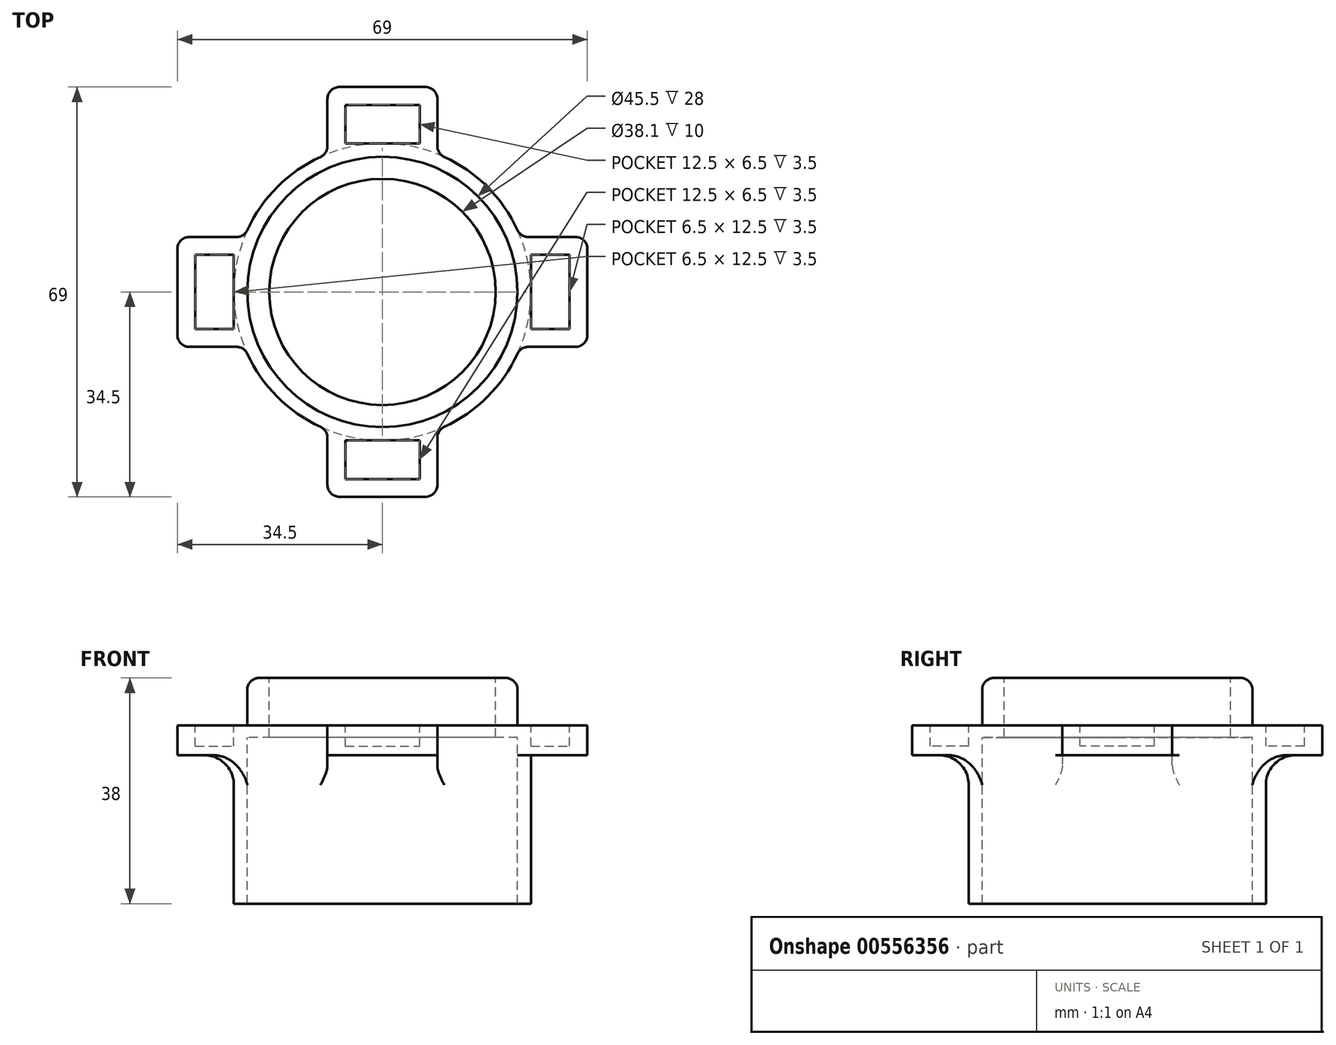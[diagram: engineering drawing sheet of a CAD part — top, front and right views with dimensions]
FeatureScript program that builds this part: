
annotation { "Feature Type Name" : "Feature", "Feature Type Description" : "" }
export const myFeature = defineFeature(function(context is Context, id is Id, definition is map)
    precondition{}
    {
        {
            var Q0;
            Q0=qCreatedBy(makeId("Top.planeOp"),FACE);
            var sketch = newSketch(context, id + "F0", { "sketchPlane" : qUnion([Q0])});
            skCircle(sketch, "E0", {"center": v(0, 0) * mm, "radius": 31.75 * mm, "construction": true});
            skCircle(sketch, "E1", {"center": v(0, 0) * mm, "radius": 22.75 * mm});
            skLineSegment(sketch, "E2.bottom", {"start": v(25, 6.25) * mm, "end": v(31.5, 6.25) * mm});
            skLineSegment(sketch, "E2.top", {"start": v(25, -6.25) * mm, "end": v(31.5, -6.25) * mm});
            skLineSegment(sketch, "E2.left", {"start": v(25, 6.25) * mm, "end": v(25, -6.25) * mm});
            skLineSegment(sketch, "E2.right", {"start": v(31.5, 6.25) * mm, "end": v(31.5, -6.25) * mm});
            skPoint(sketch, "E3", {"position": v(25, 0) * mm});
            skCircle(sketch, "E4", {"center": v(0, 0) * mm, "radius": 25 * mm});
            skLineSegment(sketch, "E5.bottom", {"start": v(-31.5, 6.25) * mm, "end": v(-25, 6.25) * mm});
            skLineSegment(sketch, "E5.top", {"start": v(-31.5, -6.25) * mm, "end": v(-25, -6.25) * mm});
            skLineSegment(sketch, "E5.left", {"start": v(-31.5, 6.25) * mm, "end": v(-31.5, -6.25) * mm});
            skLineSegment(sketch, "E5.right", {"start": v(-25, 6.25) * mm, "end": v(-25, -6.25) * mm});
            skPoint(sketch, "E6", {"position": v(-25, 0) * mm});
            skLineSegment(sketch, "E7.bottom", {"start": v(-34.5, 9.25) * mm, "end": v(34.5, 9.25) * mm});
            skLineSegment(sketch, "E7.top", {"start": v(-34.5, -9.25) * mm, "end": v(34.5, -9.25) * mm});
            skLineSegment(sketch, "E7.left", {"start": v(-34.5, 9.25) * mm, "end": v(-34.5, -9.25) * mm});
            skLineSegment(sketch, "E7.right", {"start": v(34.5, 9.25) * mm, "end": v(34.5, -9.25) * mm});
            skCircle(sketch, "E8", {"center": v(0, 0) * mm, "radius": 19.05 * mm});
            skLineSegment(sketch, "E9.bottom", {"start": v(-9.25, -34.5) * mm, "end": v(9.25, -34.5) * mm});
            skLineSegment(sketch, "E9.top", {"start": v(-9.25, 34.5) * mm, "end": v(9.25, 34.5) * mm});
            skLineSegment(sketch, "E9.left", {"start": v(-9.25, -34.5) * mm, "end": v(-9.25, 34.5) * mm});
            skLineSegment(sketch, "E9.right", {"start": v(9.25, -34.5) * mm, "end": v(9.25, 34.5) * mm});
            skLineSegment(sketch, "E10.bottom", {"start": v(-6.25, 31.5) * mm, "end": v(6.25, 31.5) * mm});
            skLineSegment(sketch, "E10.top", {"start": v(-6.25, 25) * mm, "end": v(6.25, 25) * mm});
            skLineSegment(sketch, "E10.left", {"start": v(-6.25, 31.5) * mm, "end": v(-6.25, 25) * mm});
            skLineSegment(sketch, "E10.right", {"start": v(6.25, 31.5) * mm, "end": v(6.25, 25) * mm});
            skLineSegment(sketch, "E11.bottom", {"start": v(-6.25, -25) * mm, "end": v(6.25, -25) * mm});
            skLineSegment(sketch, "E11.top", {"start": v(-6.25, -31.5) * mm, "end": v(6.25, -31.5) * mm});
            skLineSegment(sketch, "E11.left", {"start": v(-6.25, -25) * mm, "end": v(-6.25, -31.5) * mm});
            skLineSegment(sketch, "E11.right", {"start": v(6.25, -25) * mm, "end": v(6.25, -31.5) * mm});
            skPoint(sketch, "E12", {"position": v(0, 25) * mm});
            skSolve(sketch);
        }
        {
            var Q0;
            {var subQ0=sQuery(id+"F0.wireOp",EDGE,"E5.bottom");Q0=makeQuery(id+"F0.imprint","IMPRINT",FACE,{"disambiguationData":[TD([[makeQuery(id+"F0.imprint","IMPRINT",EDGE,{"derivedFrom":subQ0}),1.0]])]});}
            var Q1;
            {var subQ4=sQuery(id+"F0.wireOp",EDGE,"E2.bottom");Q1=makeQuery(id+"F0.imprint","IMPRINT",FACE,{"disambiguationData":[TD([[makeQuery(id+"F0.imprint","IMPRINT",EDGE,{"derivedFrom":subQ4}),1.0]])]});}
            var Q2;
            {var subQ0=sQuery(id+"F0.wireOp",EDGE,"E7.top");var subQ1=sQuery(id+"F0.wireOp",EDGE,"9AU1a6xc-WkkM-5iDV-fBZs-smRrCXbzpLaA");var subQ2=makeQuery(id+"F0.imprint","INTERSECT",VERTEX,{"disambiguationData":[OD(0.0)],"derivedFrom":[subQ1,subQ0]});Q2=makeQuery(id+"F0.imprint","IMPRINT",FACE,{"disambiguationData":[TD([[makeQuery(id+"F0.imprint","IMPRINT",EDGE,{"disambiguationData":[TD([[subQ2,-1.0]])],"derivedFrom":subQ1}),-1.0]])]});}
            var Q3;
            {var subQ0=sQuery(id+"F0.wireOp",EDGE,"E7.bottom");var subQ3=sQuery(id+"F0.wireOp",EDGE,"9AU1a6xc-WkkM-5iDV-fBZs-smRrCXbzpLaA");var subQ4=makeQuery(id+"F0.imprint","INTERSECT",VERTEX,{"disambiguationData":[OD(1.0)],"derivedFrom":[subQ3,subQ0]});Q3=makeQuery(id+"F0.imprint","IMPRINT",FACE,{"disambiguationData":[TD([[makeQuery(id+"F0.imprint","IMPRINT",EDGE,{"disambiguationData":[TD([[subQ4,1.0]])],"derivedFrom":subQ3}),-1.0]])]});}
            var Q4;
            {var subQ0=sQuery(id+"F0.wireOp",EDGE,"E7.bottom");var subQ1=sQuery(id+"F0.wireOp",EDGE,"9AU1a6xc-WkkM-5iDV-fBZs-smRrCXbzpLaA");var subQ2=makeQuery(id+"F0.imprint","INTERSECT",VERTEX,{"disambiguationData":[OD(0.0)],"derivedFrom":[subQ1,subQ0]});Q4=makeQuery(id+"F0.imprint","IMPRINT",FACE,{"disambiguationData":[TD([[makeQuery(id+"F0.imprint","IMPRINT",EDGE,{"disambiguationData":[TD([[subQ2,1.0]])],"derivedFrom":subQ1}),-1.0]])]});}
            var Q5;
            {var subQ0=sQuery(id+"F0.wireOp",EDGE,"E7.bottom");var subQ3=sQuery(id+"F0.wireOp",EDGE,"9AU1a6xc-WkkM-5iDV-fBZs-smRrCXbzpLaA");var subQ4=makeQuery(id+"F0.imprint","INTERSECT",VERTEX,{"disambiguationData":[OD(0.0)],"derivedFrom":[subQ3,subQ0]});Q5=makeQuery(id+"F0.imprint","IMPRINT",FACE,{"disambiguationData":[TD([[makeQuery(id+"F0.imprint","IMPRINT",EDGE,{"disambiguationData":[TD([[subQ4,-1.0]])],"derivedFrom":subQ3}),-1.0]])]});}
            var Q6;
            {var subQ0=sQuery(id+"F0.wireOp",EDGE,"E7.bottom");var subQ1=sQuery(id+"F0.wireOp",EDGE,"9AU1a6xc-WkkM-5iDV-fBZs-smRrCXbzpLaA");var subQ2=makeQuery(id+"F0.imprint","INTERSECT",VERTEX,{"disambiguationData":[OD(0.0)],"derivedFrom":[subQ1,subQ0]});Q6=makeQuery(id+"F0.imprint","IMPRINT",FACE,{"disambiguationData":[TD([[makeQuery(id+"F0.imprint","IMPRINT",EDGE,{"disambiguationData":[TD([[subQ2,-1.0]])],"derivedFrom":subQ1}),1.0]])]});}
            var Q7;
            {var subQ0=sQuery(id+"F0.wireOp",EDGE,"E7.bottom");var subQ1=sQuery(id+"F0.wireOp",EDGE,"9AU1a6xc-WkkM-5iDV-fBZs-smRrCXbzpLaA");var subQ2=makeQuery(id+"F0.imprint","INTERSECT",VERTEX,{"disambiguationData":[OD(1.0)],"derivedFrom":[subQ1,subQ0]});Q7=makeQuery(id+"F0.imprint","IMPRINT",FACE,{"disambiguationData":[TD([[makeQuery(id+"F0.imprint","IMPRINT",EDGE,{"disambiguationData":[TD([[subQ2,1.0]])],"derivedFrom":subQ1}),1.0]])]});}
            var Q8;
            {var subQ0=sQuery(id+"F0.wireOp",EDGE,"E7.bottom");var subQ1=sQuery(id+"F0.wireOp",EDGE,"9AU1a6xc-WkkM-5iDV-fBZs-smRrCXbzpLaA");var subQ2=makeQuery(id+"F0.imprint","INTERSECT",VERTEX,{"disambiguationData":[OD(0.0)],"derivedFrom":[subQ1,subQ0]});Q8=makeQuery(id+"F0.imprint","IMPRINT",FACE,{"disambiguationData":[TD([[makeQuery(id+"F0.imprint","IMPRINT",EDGE,{"disambiguationData":[TD([[subQ2,1.0]])],"derivedFrom":subQ1}),1.0]])]});}
            var Q9;
            {var subQ0=sQuery(id+"F0.wireOp",EDGE,"E7.top");var subQ1=sQuery(id+"F0.wireOp",EDGE,"9AU1a6xc-WkkM-5iDV-fBZs-smRrCXbzpLaA");var subQ2=makeQuery(id+"F0.imprint","INTERSECT",VERTEX,{"disambiguationData":[OD(0.0)],"derivedFrom":[subQ1,subQ0]});Q9=makeQuery(id+"F0.imprint","IMPRINT",FACE,{"disambiguationData":[TD([[makeQuery(id+"F0.imprint","IMPRINT",EDGE,{"disambiguationData":[TD([[subQ2,-1.0]])],"derivedFrom":subQ1}),1.0]])]});}
            var Q10;
            {var subQ1=sQuery(id+"F0.wireOp",EDGE,"E5.bottom");Q10=makeQuery(id+"F0.imprint","IMPRINT",FACE,{"disambiguationData":[TD([[makeQuery(id+"F0.imprint","IMPRINT",EDGE,{"derivedFrom":subQ1}),-1.0]])]});}
            var Q11;
            {var subQ3=sQuery(id+"F0.wireOp",EDGE,"E2.bottom");Q11=makeQuery(id+"F0.imprint","IMPRINT",FACE,{"disambiguationData":[TD([[makeQuery(id+"F0.imprint","IMPRINT",EDGE,{"derivedFrom":subQ3}),-1.0]])]});}
            var Q12;
            {var subQ0=sQuery(id+"F0.wireOp",EDGE,"E7.bottom");var subQ1=sQuery(id+"F0.wireOp",EDGE,"E1");var subQ2=makeQuery(id+"F0.imprint","INTERSECT",VERTEX,{"disambiguationData":[OD(0.0)],"derivedFrom":[subQ1,subQ0]});Q12=makeQuery(id+"F0.imprint","IMPRINT",FACE,{"disambiguationData":[TD([[makeQuery(id+"F0.imprint","IMPRINT",EDGE,{"disambiguationData":[TD([[subQ2,1.0]])],"derivedFrom":subQ1}),-1.0]])]});}
            var Q13;
            {var subQ4=sQuery(id+"F0.wireOp",EDGE,"E7.bottom");var subQ5=sQuery(id+"F0.wireOp",EDGE,"E1");var subQ6=makeQuery(id+"F0.imprint","INTERSECT",VERTEX,{"disambiguationData":[OD(0.0)],"derivedFrom":[subQ5,subQ4]});Q13=makeQuery(id+"F0.imprint","IMPRINT",FACE,{"disambiguationData":[TD([[makeQuery(id+"F0.imprint","IMPRINT",EDGE,{"disambiguationData":[TD([[subQ6,-1.0]])],"derivedFrom":subQ5}),-1.0]])]});}
            var Q14;
            {var subQ4=sQuery(id+"F0.wireOp",EDGE,"E7.bottom");var subQ5=sQuery(id+"F0.wireOp",EDGE,"E1");var subQ6=makeQuery(id+"F0.imprint","INTERSECT",VERTEX,{"disambiguationData":[OD(1.0)],"derivedFrom":[subQ5,subQ4]});Q14=makeQuery(id+"F0.imprint","IMPRINT",FACE,{"disambiguationData":[TD([[makeQuery(id+"F0.imprint","IMPRINT",EDGE,{"disambiguationData":[TD([[subQ6,1.0]])],"derivedFrom":subQ5}),-1.0]])]});}
            var Q15;
            {var subQ0=sQuery(id+"F0.wireOp",EDGE,"E7.top");var subQ1=sQuery(id+"F0.wireOp",EDGE,"E1");var subQ2=makeQuery(id+"F0.imprint","INTERSECT",VERTEX,{"disambiguationData":[OD(0.0)],"derivedFrom":[subQ1,subQ0]});Q15=makeQuery(id+"F0.imprint","IMPRINT",FACE,{"disambiguationData":[TD([[makeQuery(id+"F0.imprint","IMPRINT",EDGE,{"disambiguationData":[TD([[subQ2,-1.0]])],"derivedFrom":subQ1}),-1.0]])]});}
            var Q16;
            {var subQ0=sQuery(id+"F0.wireOp",EDGE,"E7.bottom");var subQ3=sQuery(id+"F0.wireOp",EDGE,"E1");var subQ4=makeQuery(id+"F0.imprint","INTERSECT",VERTEX,{"disambiguationData":[OD(1.0)],"derivedFrom":[subQ3,subQ0]});Q16=makeQuery(id+"F0.imprint","IMPRINT",FACE,{"disambiguationData":[TD([[makeQuery(id+"F0.imprint","IMPRINT",EDGE,{"disambiguationData":[TD([[subQ4,-1.0]])],"derivedFrom":subQ3}),-1.0]])]});}
            var Q17;
            {var subQ1=sQuery(id+"F0.wireOp",EDGE,"E9.top");Q17=makeQuery(id+"F0.imprint","IMPRINT",FACE,{"disambiguationData":[TD([[makeQuery(id+"F0.imprint","IMPRINT",EDGE,{"derivedFrom":subQ1}),-1.0]])]});}
            var Q18;
            Q18=makeQuery(id+"F0.imprint","IMPRINT",FACE,{"disambiguationData":[TD([[makeQuery(id+"F0.imprint","IMPRINT",EDGE,{"derivedFrom":sQuery(id+"F0.wireOp",EDGE,"E10.bottom")}),-1.0]])]});
            var Q19;
            {var subQ3=sQuery(id+"F0.wireOp",EDGE,"E1");var subQ5=sQuery(id+"F0.wireOp",EDGE,"E9.right");var subQ6=makeQuery(id+"F0.imprint","INTERSECT",VERTEX,{"disambiguationData":[OD(0.0)],"derivedFrom":[subQ3,subQ5]});Q19=makeQuery(id+"F0.imprint","IMPRINT",FACE,{"disambiguationData":[TD([[makeQuery(id+"F0.imprint","IMPRINT",EDGE,{"disambiguationData":[TD([[subQ6,-1.0]])],"derivedFrom":subQ3}),-1.0]])]});}
            var Q20;
            {var subQ0=sQuery(id+"F0.wireOp",EDGE,"E9.right");var subQ1=sQuery(id+"F0.wireOp",EDGE,"E1");var subQ2=makeQuery(id+"F0.imprint","INTERSECT",VERTEX,{"disambiguationData":[OD(1.0)],"derivedFrom":[subQ1,subQ0]});Q20=makeQuery(id+"F0.imprint","IMPRINT",FACE,{"disambiguationData":[TD([[makeQuery(id+"F0.imprint","IMPRINT",EDGE,{"disambiguationData":[TD([[subQ2,-1.0]])],"derivedFrom":subQ1}),-1.0]])]});}
            var Q21;
            {var subQ4=sQuery(id+"F0.wireOp",EDGE,"E9.left");var subQ6=sQuery(id+"F0.wireOp",EDGE,"E1");var subQ7=makeQuery(id+"F0.imprint","INTERSECT",VERTEX,{"disambiguationData":[OD(1.0)],"derivedFrom":[subQ6,subQ4]});Q21=makeQuery(id+"F0.imprint","IMPRINT",FACE,{"disambiguationData":[TD([[makeQuery(id+"F0.imprint","IMPRINT",EDGE,{"disambiguationData":[TD([[subQ7,-1.0]])],"derivedFrom":subQ6}),-1.0]])]});}
            var Q22;
            {var subQ1=sQuery(id+"F0.wireOp",EDGE,"E9.bottom");Q22=makeQuery(id+"F0.imprint","IMPRINT",FACE,{"disambiguationData":[TD([[makeQuery(id+"F0.imprint","IMPRINT",EDGE,{"derivedFrom":subQ1}),1.0]])]});}
            var Q23;
            Q23=makeQuery(id+"F0.imprint","IMPRINT",FACE,{"disambiguationData":[TD([[makeQuery(id+"F0.imprint","IMPRINT",EDGE,{"derivedFrom":sQuery(id+"F0.wireOp",EDGE,"E11.top")}),1.0]])]});
            extrude(context, id + "F1", {"entities" : qUnion([Q0, Q1, Q2, Q3, Q4, Q5, Q6, Q7, Q8, Q9, Q10, Q11, Q12, Q13, Q14, Q15, Q16, Q17, Q18, Q19, Q20, Q21, Q22, Q23]), "oppositeDirection" : true, "depth" : 5 * mm, "offsetDistance" : 25 * mm});
        }
        {
            var Q0;
            {var subQ0=sQuery(id+"F0.wireOp",EDGE,"E7.bottom");var subQ1=sQuery(id+"F0.wireOp",EDGE,"E1");var subQ2=makeQuery(id+"F0.imprint","INTERSECT",VERTEX,{"disambiguationData":[OD(0.0)],"derivedFrom":[subQ1,subQ0]});Q0=makeQuery(id+"F0.imprint","IMPRINT",FACE,{"disambiguationData":[TD([[makeQuery(id+"F0.imprint","IMPRINT",EDGE,{"disambiguationData":[TD([[subQ2,1.0]])],"derivedFrom":subQ1}),1.0]])]});}
            var Q1;
            {var subQ0=sQuery(id+"F0.wireOp",EDGE,"E7.bottom");var subQ1=sQuery(id+"F0.wireOp",EDGE,"E1");var subQ2=makeQuery(id+"F0.imprint","INTERSECT",VERTEX,{"disambiguationData":[OD(0.0)],"derivedFrom":[subQ1,subQ0]});Q1=makeQuery(id+"F0.imprint","IMPRINT",FACE,{"disambiguationData":[TD([[makeQuery(id+"F0.imprint","IMPRINT",EDGE,{"disambiguationData":[TD([[subQ2,-1.0]])],"derivedFrom":subQ1}),1.0]])]});}
            var Q2;
            {var subQ0=sQuery(id+"F0.wireOp",EDGE,"E7.top");var subQ1=sQuery(id+"F0.wireOp",EDGE,"E1");var subQ2=makeQuery(id+"F0.imprint","INTERSECT",VERTEX,{"disambiguationData":[OD(0.0)],"derivedFrom":[subQ1,subQ0]});Q2=makeQuery(id+"F0.imprint","IMPRINT",FACE,{"disambiguationData":[TD([[makeQuery(id+"F0.imprint","IMPRINT",EDGE,{"disambiguationData":[TD([[subQ2,-1.0]])],"derivedFrom":subQ1}),1.0]])]});}
            var Q3;
            {var subQ0=sQuery(id+"F0.wireOp",EDGE,"E7.bottom");var subQ1=sQuery(id+"F0.wireOp",EDGE,"E1");var subQ2=makeQuery(id+"F0.imprint","INTERSECT",VERTEX,{"disambiguationData":[OD(1.0)],"derivedFrom":[subQ1,subQ0]});Q3=makeQuery(id+"F0.imprint","IMPRINT",FACE,{"disambiguationData":[TD([[makeQuery(id+"F0.imprint","IMPRINT",EDGE,{"disambiguationData":[TD([[subQ2,1.0]])],"derivedFrom":subQ1}),1.0]])]});}
            var Q4;
            {var subQ0=sQuery(id+"F0.wireOp",EDGE,"E9.right");var subQ1=sQuery(id+"F0.wireOp",EDGE,"E1");var subQ2=makeQuery(id+"F0.imprint","INTERSECT",VERTEX,{"disambiguationData":[OD(1.0)],"derivedFrom":[subQ1,subQ0]});Q4=makeQuery(id+"F0.imprint","IMPRINT",FACE,{"disambiguationData":[TD([[makeQuery(id+"F0.imprint","IMPRINT",EDGE,{"disambiguationData":[TD([[subQ2,-1.0]])],"derivedFrom":subQ1}),1.0]])]});}
            var Q5;
            {var subQ0=sQuery(id+"F0.wireOp",EDGE,"E9.left");var subQ1=sQuery(id+"F0.wireOp",EDGE,"E1");var subQ2=makeQuery(id+"F0.imprint","INTERSECT",VERTEX,{"disambiguationData":[OD(1.0)],"derivedFrom":[subQ1,subQ0]});Q5=makeQuery(id+"F0.imprint","IMPRINT",FACE,{"disambiguationData":[TD([[makeQuery(id+"F0.imprint","IMPRINT",EDGE,{"disambiguationData":[TD([[subQ2,-1.0]])],"derivedFrom":subQ1}),1.0]])]});}
            var Q6;
            {var subQ0=sQuery(id+"F0.wireOp",EDGE,"E9.right");var subQ1=sQuery(id+"F0.wireOp",EDGE,"E1");var subQ2=makeQuery(id+"F0.imprint","INTERSECT",VERTEX,{"disambiguationData":[OD(0.0)],"derivedFrom":[subQ1,subQ0]});Q6=makeQuery(id+"F0.imprint","IMPRINT",FACE,{"disambiguationData":[TD([[makeQuery(id+"F0.imprint","IMPRINT",EDGE,{"disambiguationData":[TD([[subQ2,-1.0]])],"derivedFrom":subQ1}),1.0]])]});}
            var Q7;
            {var subQ0=sQuery(id+"F0.wireOp",EDGE,"E7.bottom");var subQ1=sQuery(id+"F0.wireOp",EDGE,"E1");var subQ2=makeQuery(id+"F0.imprint","INTERSECT",VERTEX,{"disambiguationData":[OD(1.0)],"derivedFrom":[subQ1,subQ0]});Q7=makeQuery(id+"F0.imprint","IMPRINT",FACE,{"disambiguationData":[TD([[makeQuery(id+"F0.imprint","IMPRINT",EDGE,{"disambiguationData":[TD([[subQ2,-1.0]])],"derivedFrom":subQ1}),1.0]])]});}
            extrude(context, id + "F2", {"entities" : qUnion([Q0, Q1, Q2, Q3, Q4, Q5, Q6, Q7]), "operationType" : NewBodyOperationType.ADD, "oppositeDirection" : true, "depth" : 2 * mm, "offsetDistance" : 25 * mm});
        }
        {
            var Q0;
            {var subQ1=sQuery(id+"F0.wireOp",EDGE,"E5.bottom");Q0=makeQuery(id+"F0.imprint","IMPRINT",FACE,{"disambiguationData":[TD([[makeQuery(id+"F0.imprint","IMPRINT",EDGE,{"derivedFrom":subQ1}),-1.0]])]});}
            var Q1;
            {var subQ3=sQuery(id+"F0.wireOp",EDGE,"E2.bottom");Q1=makeQuery(id+"F0.imprint","IMPRINT",FACE,{"disambiguationData":[TD([[makeQuery(id+"F0.imprint","IMPRINT",EDGE,{"derivedFrom":subQ3}),-1.0]])]});}
            var Q2;
            Q2=makeQuery(id+"F0.imprint","IMPRINT",FACE,{"disambiguationData":[TD([[makeQuery(id+"F0.imprint","IMPRINT",EDGE,{"derivedFrom":sQuery(id+"F0.wireOp",EDGE,"E11.top")}),1.0]])]});
            var Q3;
            Q3=makeQuery(id+"F0.imprint","IMPRINT",FACE,{"disambiguationData":[TD([[makeQuery(id+"F0.imprint","IMPRINT",EDGE,{"derivedFrom":sQuery(id+"F0.wireOp",EDGE,"E10.bottom")}),-1.0]])]});
            extrude(context, id + "F3", {"entities" : qUnion([Q0, Q1, Q2, Q3]), "operationType" : NewBodyOperationType.REMOVE, "oppositeDirection" : true, "depth" : 3.5 * mm, "offsetDistance" : 25 * mm});
        }
        {
            var Q0;
            {var subQ0=sQuery(id+"F0.wireOp",EDGE,"E7.bottom");var subQ1=sQuery(id+"F0.wireOp",EDGE,"E1");var subQ2=makeQuery(id+"F0.imprint","INTERSECT",VERTEX,{"disambiguationData":[OD(0.0)],"derivedFrom":[subQ1,subQ0]});Q0=makeQuery(id+"F0.imprint","IMPRINT",FACE,{"disambiguationData":[TD([[makeQuery(id+"F0.imprint","IMPRINT",EDGE,{"disambiguationData":[TD([[subQ2,1.0]])],"derivedFrom":subQ1}),1.0]])]});}
            var Q1;
            {var subQ0=sQuery(id+"F0.wireOp",EDGE,"E7.bottom");var subQ1=sQuery(id+"F0.wireOp",EDGE,"E1");var subQ2=makeQuery(id+"F0.imprint","INTERSECT",VERTEX,{"disambiguationData":[OD(0.0)],"derivedFrom":[subQ1,subQ0]});Q1=makeQuery(id+"F0.imprint","IMPRINT",FACE,{"disambiguationData":[TD([[makeQuery(id+"F0.imprint","IMPRINT",EDGE,{"disambiguationData":[TD([[subQ2,-1.0]])],"derivedFrom":subQ1}),1.0]])]});}
            var Q2;
            {var subQ0=sQuery(id+"F0.wireOp",EDGE,"E7.bottom");var subQ1=sQuery(id+"F0.wireOp",EDGE,"E1");var subQ2=makeQuery(id+"F0.imprint","INTERSECT",VERTEX,{"disambiguationData":[OD(1.0)],"derivedFrom":[subQ1,subQ0]});Q2=makeQuery(id+"F0.imprint","IMPRINT",FACE,{"disambiguationData":[TD([[makeQuery(id+"F0.imprint","IMPRINT",EDGE,{"disambiguationData":[TD([[subQ2,1.0]])],"derivedFrom":subQ1}),1.0]])]});}
            var Q3;
            {var subQ0=sQuery(id+"F0.wireOp",EDGE,"E7.top");var subQ1=sQuery(id+"F0.wireOp",EDGE,"E1");var subQ2=makeQuery(id+"F0.imprint","INTERSECT",VERTEX,{"disambiguationData":[OD(0.0)],"derivedFrom":[subQ1,subQ0]});Q3=makeQuery(id+"F0.imprint","IMPRINT",FACE,{"disambiguationData":[TD([[makeQuery(id+"F0.imprint","IMPRINT",EDGE,{"disambiguationData":[TD([[subQ2,-1.0]])],"derivedFrom":subQ1}),1.0]])]});}
            var Q4;
            {var subQ0=sQuery(id+"F0.wireOp",EDGE,"E7.bottom");var subQ1=sQuery(id+"F0.wireOp",EDGE,"E1");var subQ2=makeQuery(id+"F0.imprint","INTERSECT",VERTEX,{"disambiguationData":[OD(1.0)],"derivedFrom":[subQ1,subQ0]});Q4=makeQuery(id+"F0.imprint","IMPRINT",FACE,{"disambiguationData":[TD([[makeQuery(id+"F0.imprint","IMPRINT",EDGE,{"disambiguationData":[TD([[subQ2,-1.0]])],"derivedFrom":subQ1}),1.0]])]});}
            var Q5;
            {var subQ0=sQuery(id+"F0.wireOp",EDGE,"E9.left");var subQ1=sQuery(id+"F0.wireOp",EDGE,"E1");var subQ2=makeQuery(id+"F0.imprint","INTERSECT",VERTEX,{"disambiguationData":[OD(1.0)],"derivedFrom":[subQ1,subQ0]});Q5=makeQuery(id+"F0.imprint","IMPRINT",FACE,{"disambiguationData":[TD([[makeQuery(id+"F0.imprint","IMPRINT",EDGE,{"disambiguationData":[TD([[subQ2,-1.0]])],"derivedFrom":subQ1}),1.0]])]});}
            var Q6;
            {var subQ0=sQuery(id+"F0.wireOp",EDGE,"E9.right");var subQ1=sQuery(id+"F0.wireOp",EDGE,"E1");var subQ2=makeQuery(id+"F0.imprint","INTERSECT",VERTEX,{"disambiguationData":[OD(1.0)],"derivedFrom":[subQ1,subQ0]});Q6=makeQuery(id+"F0.imprint","IMPRINT",FACE,{"disambiguationData":[TD([[makeQuery(id+"F0.imprint","IMPRINT",EDGE,{"disambiguationData":[TD([[subQ2,-1.0]])],"derivedFrom":subQ1}),1.0]])]});}
            var Q7;
            {var subQ0=sQuery(id+"F0.wireOp",EDGE,"E9.right");var subQ1=sQuery(id+"F0.wireOp",EDGE,"E1");var subQ2=makeQuery(id+"F0.imprint","INTERSECT",VERTEX,{"disambiguationData":[OD(0.0)],"derivedFrom":[subQ1,subQ0]});Q7=makeQuery(id+"F0.imprint","IMPRINT",FACE,{"disambiguationData":[TD([[makeQuery(id+"F0.imprint","IMPRINT",EDGE,{"disambiguationData":[TD([[subQ2,-1.0]])],"derivedFrom":subQ1}),1.0]])]});}
            extrude(context, id + "F4", {"entities" : qUnion([Q0, Q1, Q2, Q3, Q4, Q5, Q6, Q7]), "operationType" : NewBodyOperationType.ADD, "depth" : 8 * mm, "offsetDistance" : 25 * mm});
        }
        {
            var Q0;
            Q0=makeQuery(id+"F1.opExtrude","SWEPT_EDGE",EDGE,{"disambiguationData":[OSD([sQuery(id+"F0.wireOp",EDGE,"E7.bottom"),sQuery(id+"F0.wireOp",EDGE,"E7.left")])]});
            var Q1;
            {var subQ0=sQuery(id+"F0.wireOp",EDGE,"E7.bottom");var subQ1=sQuery(id+"F0.wireOp",EDGE,"E4");Q1=makeQuery(id+"F1.opExtrude","SWEPT_EDGE",EDGE,{"disambiguationData":[OSD([subQ1,subQ0]),TDD([makeQuery(id+"F0.imprint","INTERSECT",VERTEX,{"disambiguationData":[OD(1.0)],"derivedFrom":[subQ1,subQ0]})])]});}
            var Q2;
            Q2=makeQuery(id+"F1.opExtrude","SWEPT_EDGE",EDGE,{"disambiguationData":[OSD([sQuery(id+"F0.wireOp",EDGE,"E7.top"),sQuery(id+"F0.wireOp",EDGE,"E7.left")])]});
            var Q3;
            Q3=makeQuery(id+"F1.opExtrude","SWEPT_EDGE",EDGE,{"disambiguationData":[OSD([sQuery(id+"F0.wireOp",EDGE,"E7.bottom"),sQuery(id+"F0.wireOp",EDGE,"E7.right")])]});
            var Q4;
            {var subQ0=sQuery(id+"F0.wireOp",EDGE,"E7.top");var subQ1=sQuery(id+"F0.wireOp",EDGE,"E4");Q4=makeQuery(id+"F1.opExtrude","SWEPT_EDGE",EDGE,{"disambiguationData":[OSD([subQ1,subQ0]),TDD([makeQuery(id+"F0.imprint","INTERSECT",VERTEX,{"disambiguationData":[OD(1.0)],"derivedFrom":[subQ1,subQ0]})])]});}
            var Q5;
            Q5=makeQuery(id+"F1.opExtrude","SWEPT_EDGE",EDGE,{"disambiguationData":[OSD([sQuery(id+"F0.wireOp",EDGE,"E7.top"),sQuery(id+"F0.wireOp",EDGE,"E7.right")])]});
            var Q6;
            {var subQ0=sQuery(id+"F0.wireOp",EDGE,"E7.top");var subQ1=sQuery(id+"F0.wireOp",EDGE,"E4");Q6=makeQuery(id+"F1.opExtrude","SWEPT_EDGE",EDGE,{"disambiguationData":[OSD([subQ1,subQ0]),TDD([makeQuery(id+"F0.imprint","INTERSECT",VERTEX,{"disambiguationData":[OD(0.0)],"derivedFrom":[subQ1,subQ0]})])]});}
            var Q7;
            {var subQ0=sQuery(id+"F0.wireOp",EDGE,"E7.bottom");var subQ1=sQuery(id+"F0.wireOp",EDGE,"E4");Q7=makeQuery(id+"F1.opExtrude","SWEPT_EDGE",EDGE,{"disambiguationData":[OSD([subQ1,subQ0]),TDD([makeQuery(id+"F0.imprint","INTERSECT",VERTEX,{"disambiguationData":[OD(0.0)],"derivedFrom":[subQ1,subQ0]})])]});}
            var Q8;
            Q8=makeQuery(id+"F4.opExtrude","CAP_EDGE",EDGE,{"disambiguationData":[OSD([sQuery(id+"F0.wireOp",EDGE,"E1")])],"isStart":false});
            var Q9;
            Q9=makeQuery(id+"F1.opExtrude","SWEPT_EDGE",EDGE,{"disambiguationData":[OSD([sQuery(id+"F0.wireOp",EDGE,"E9.top"),sQuery(id+"F0.wireOp",EDGE,"E9.left")])]});
            var Q10;
            Q10=makeQuery(id+"F1.opExtrude","SWEPT_EDGE",EDGE,{"disambiguationData":[OSD([sQuery(id+"F0.wireOp",EDGE,"E9.top"),sQuery(id+"F0.wireOp",EDGE,"E9.right")])]});
            var Q11;
            Q11=makeQuery(id+"F1.opExtrude","SWEPT_EDGE",EDGE,{"disambiguationData":[OSD([sQuery(id+"F0.wireOp",EDGE,"E9.bottom"),sQuery(id+"F0.wireOp",EDGE,"E9.left")])]});
            var Q12;
            Q12=makeQuery(id+"F1.opExtrude","SWEPT_EDGE",EDGE,{"disambiguationData":[OSD([sQuery(id+"F0.wireOp",EDGE,"E9.bottom"),sQuery(id+"F0.wireOp",EDGE,"E9.right")])]});
            var Q13;
            {var subQ0=sQuery(id+"F0.wireOp",EDGE,"E9.right");var subQ1=sQuery(id+"F0.wireOp",EDGE,"E4");Q13=makeQuery(id+"F1.opExtrude","SWEPT_EDGE",EDGE,{"disambiguationData":[OSD([subQ1,subQ0]),TDD([makeQuery(id+"F0.imprint","INTERSECT",VERTEX,{"disambiguationData":[OD(1.0)],"derivedFrom":[subQ1,subQ0]})])]});}
            var Q14;
            {var subQ0=sQuery(id+"F0.wireOp",EDGE,"E9.left");var subQ1=sQuery(id+"F0.wireOp",EDGE,"E4");Q14=makeQuery(id+"F1.opExtrude","SWEPT_EDGE",EDGE,{"disambiguationData":[OSD([subQ1,subQ0]),TDD([makeQuery(id+"F0.imprint","INTERSECT",VERTEX,{"disambiguationData":[OD(1.0)],"derivedFrom":[subQ1,subQ0]})])]});}
            var Q15;
            {var subQ0=sQuery(id+"F0.wireOp",EDGE,"E9.left");var subQ1=sQuery(id+"F0.wireOp",EDGE,"E4");Q15=makeQuery(id+"F1.opExtrude","SWEPT_EDGE",EDGE,{"disambiguationData":[OSD([subQ1,subQ0]),TDD([makeQuery(id+"F0.imprint","INTERSECT",VERTEX,{"disambiguationData":[OD(0.0)],"derivedFrom":[subQ1,subQ0]})])]});}
            var Q16;
            {var subQ0=sQuery(id+"F0.wireOp",EDGE,"E9.right");var subQ1=sQuery(id+"F0.wireOp",EDGE,"E4");Q16=makeQuery(id+"F1.opExtrude","SWEPT_EDGE",EDGE,{"disambiguationData":[OSD([subQ1,subQ0]),TDD([makeQuery(id+"F0.imprint","INTERSECT",VERTEX,{"disambiguationData":[OD(0.0)],"derivedFrom":[subQ1,subQ0]})])]});}
            fillet(context, id + "F5", {"entities" : qUnion([Q0, Q1, Q2, Q3, Q4, Q5, Q6, Q7, Q8, Q9, Q10, Q11, Q12, Q13, Q14, Q15, Q16]), "radius" : 2 * mm, "tangentPropagation" : true, "allowEdgeOverflow" : false});
        }
        {
            var Q0;
            Q0=makeQuery(id+"F1.opExtrude","CAP_FACE",FACE,{"disambiguationData":[OSD([sQuery(id+"F0.wireOp",EDGE,"E1"),sQuery(id+"F0.wireOp",EDGE,"E4"),sQuery(id+"F0.wireOp",EDGE,"E7.bottom"),sQuery(id+"F0.wireOp",EDGE,"E7.top"),sQuery(id+"F0.wireOp",EDGE,"E7.left"),sQuery(id+"F0.wireOp",EDGE,"E7.right")])],"isStart":false});
            var sketch = newSketch(context, id + "F6", { "sketchPlane" : qUnion([Q0])});
            skCircle(sketch, "E13", {"center": v(0, 0) * mm, "radius": 25 * mm});
            skCircle(sketch, "E14", {"center": v(0, 0) * mm, "radius": 22.75 * mm});
            skSolve(sketch);
        }
        {
            var Q0;
            Q0=makeQuery(id+"F6.imprint","IMPRINT",FACE,{"disambiguationData":[TD([[makeQuery(id+"F6.imprint","IMPRINT",EDGE,{"derivedFrom":sQuery(id+"F6.wireOp",EDGE,"E14")}),1.0]])]});
            extrude(context, id + "F7", {"entities" : qUnion([Q0]), "operationType" : NewBodyOperationType.ADD, "depth" : 25 * mm, "offsetDistance" : 25 * mm});
        }
        {
            var Q0;
            {var subQ1=sQuery(id+"F0.wireOp",EDGE,"E4");var subQ5=sQuery(id+"F0.wireOp",EDGE,"E9.right");var subQ6=makeQuery(id+"F0.imprint","INTERSECT",VERTEX,{"disambiguationData":[OD(0.0)],"derivedFrom":[subQ1,subQ5]});var subQ7=sQuery(id+"F6.wireOp",EDGE,"E13");Q0=makeQuery(id+"F7.boolean.opBoolean","SPLIT",EDGE,{"disambiguationData":[TD([makeQuery(id+"F5.opFillet","BLEND_FACE",FACE,{"disambiguationData":[OSD([subQ1,subQ5]),TDD([makeQuery(id+"F1.opExtrude","SWEPT_EDGE",EDGE,{"disambiguationData":[OSD([subQ1,subQ5]),TDD([subQ6])]})])]})])],"derivedFrom":makeQuery(id+"F7.opExtrude","CAP_EDGE",EDGE,{"disambiguationData":[OSD([subQ7])],"isStart":true})});}
            var Q1;
            {var subQ1=sQuery(id+"F0.wireOp",EDGE,"E4");var subQ3=sQuery(id+"F0.wireOp",EDGE,"E7.bottom");var subQ4=makeQuery(id+"F0.imprint","INTERSECT",VERTEX,{"disambiguationData":[OD(0.0)],"derivedFrom":[subQ1,subQ3]});var subQ7=sQuery(id+"F6.wireOp",EDGE,"E13");Q1=makeQuery(id+"F7.boolean.opBoolean","SPLIT",EDGE,{"disambiguationData":[TD([makeQuery(id+"F5.opFillet","BLEND_FACE",FACE,{"disambiguationData":[OSD([subQ1,subQ3]),TDD([makeQuery(id+"F1.opExtrude","SWEPT_EDGE",EDGE,{"disambiguationData":[OSD([subQ1,subQ3]),TDD([subQ4])]})])]})])],"derivedFrom":makeQuery(id+"F7.opExtrude","CAP_EDGE",EDGE,{"disambiguationData":[OSD([subQ7])],"isStart":true})});}
            var Q2;
            {var subQ1=sQuery(id+"F0.wireOp",EDGE,"E4");var subQ4=sQuery(id+"F0.wireOp",EDGE,"E7.bottom");var subQ5=makeQuery(id+"F0.imprint","INTERSECT",VERTEX,{"disambiguationData":[OD(1.0)],"derivedFrom":[subQ1,subQ4]});var subQ7=sQuery(id+"F6.wireOp",EDGE,"E13");Q2=makeQuery(id+"F7.boolean.opBoolean","SPLIT",EDGE,{"disambiguationData":[TD([makeQuery(id+"F5.opFillet","BLEND_FACE",FACE,{"disambiguationData":[OSD([subQ1,subQ4]),TDD([makeQuery(id+"F1.opExtrude","SWEPT_EDGE",EDGE,{"disambiguationData":[OSD([subQ1,subQ4]),TDD([subQ5])]})])]})])],"derivedFrom":makeQuery(id+"F7.opExtrude","CAP_EDGE",EDGE,{"disambiguationData":[OSD([subQ7])],"isStart":true})});}
            var Q3;
            {var subQ1=sQuery(id+"F0.wireOp",EDGE,"E4");var subQ2=sQuery(id+"F0.wireOp",EDGE,"E9.left");var subQ3=makeQuery(id+"F0.imprint","INTERSECT",VERTEX,{"disambiguationData":[OD(1.0)],"derivedFrom":[subQ1,subQ2]});var subQ7=sQuery(id+"F6.wireOp",EDGE,"E13");Q3=makeQuery(id+"F7.boolean.opBoolean","SPLIT",EDGE,{"disambiguationData":[TD([makeQuery(id+"F5.opFillet","BLEND_FACE",FACE,{"disambiguationData":[OSD([subQ1,subQ2]),TDD([makeQuery(id+"F1.opExtrude","SWEPT_EDGE",EDGE,{"disambiguationData":[OSD([subQ1,subQ2]),TDD([subQ3])]})])]})])],"derivedFrom":makeQuery(id+"F7.opExtrude","CAP_EDGE",EDGE,{"disambiguationData":[OSD([subQ7])],"isStart":true})});}
            fillet(context, id + "F8", {"entities" : qUnion([Q0, Q1, Q2, Q3]), "radius" : 5 * mm, "tangentPropagation" : true, "allowEdgeOverflow" : false});
        }
    });
